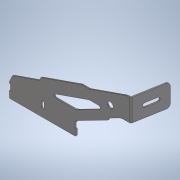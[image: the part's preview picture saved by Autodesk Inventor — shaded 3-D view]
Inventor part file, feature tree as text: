
AUTODESK INVENTOR PART (.ipt)
format: ipt  version: 2020 (Build 240168000, 168)  size: 588,288 bytes
history: native  units: mm
features: other x3, extrude x1, plane x1
ambient origin geometry x8: Origin, YZ Plane, XZ Plane, XY Plane, X Axis, Y Axis, Z Axis, Center Point
bodies: Body1 (feature_tree)
feature tree (5):
  other  "實體1"
  extrude  "擠出1"  Depth=130.0mm
  other  "折彎零件1"
  plane  "工作平面1"
  other  "定義1"
